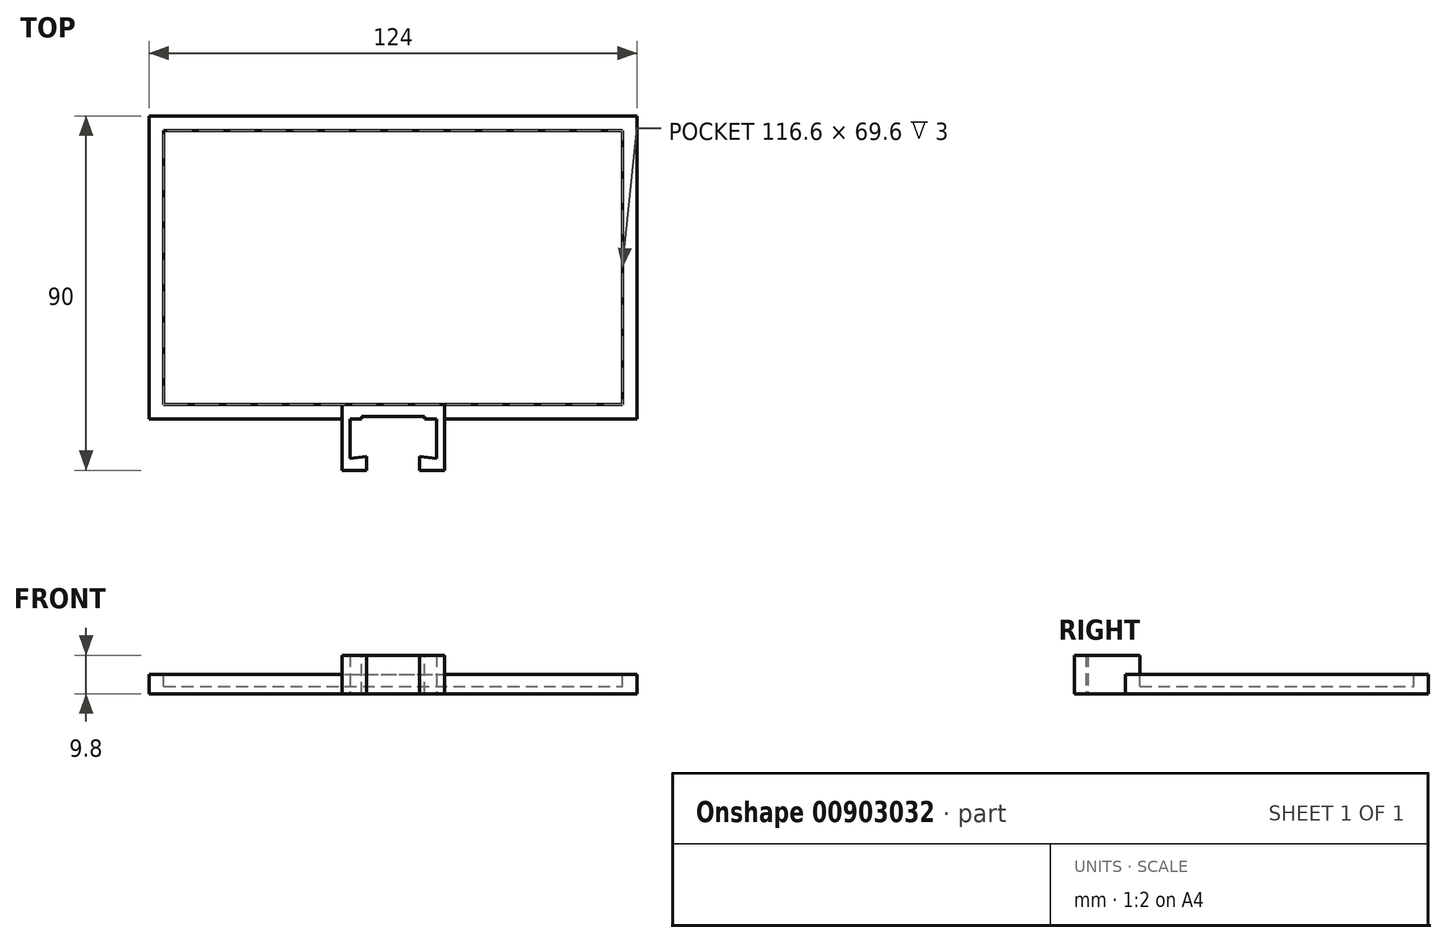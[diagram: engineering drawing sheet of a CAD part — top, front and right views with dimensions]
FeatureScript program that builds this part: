
annotation { "Feature Type Name" : "Feature", "Feature Type Description" : "" }
export const myFeature = defineFeature(function(context is Context, id is Id, definition is map)
    precondition{}
    {
        {
            var Q0;
            Q0=qCreatedBy(makeId("Top.planeOp"),FACE);
            var sketch = newSketch(context, id + "F0", { "sketchPlane" : qUnion([Q0])});
            skLineSegment(sketch, "E0.bottom", {"start": v(0, 0) * mm, "end": v(124, 0) * mm});
            skLineSegment(sketch, "E0.top", {"start": v(0, 77) * mm, "end": v(124, 77) * mm});
            skLineSegment(sketch, "E0.left", {"start": v(0, 0) * mm, "end": v(0, 77) * mm});
            skLineSegment(sketch, "E0.right", {"start": v(124, 0) * mm, "end": v(124, 77) * mm});
            skSolve(sketch);
        }
        {
            var Q0;
            Q0=makeQuery(id+"F0.imprint","IMPRINT",FACE,{"disambiguationData":[TD([[makeQuery(id+"F0.imprint","IMPRINT",EDGE,{"derivedFrom":sQuery(id+"F0.wireOp",EDGE,"E0.bottom")}),1.0]])]});
            extrude(context, id + "F1", {"entities" : qUnion([Q0]), "depth" : 4.9 * mm, "offsetDistance" : 25 * mm});
        }
        {
            var Q0;
            Q0=makeQuery(id+"F1.opExtrude","CAP_FACE",FACE,{"disambiguationData":[OSD([sQuery(id+"F0.wireOp",EDGE,"E0.bottom"),sQuery(id+"F0.wireOp",EDGE,"E0.top"),sQuery(id+"F0.wireOp",EDGE,"E0.left"),sQuery(id+"F0.wireOp",EDGE,"E0.right")])],"isStart":false});
            var sketch = newSketch(context, id + "F2", { "sketchPlane" : qUnion([Q0])});
            skLineSegment(sketch, "E1.0", {"start": v(3.7, 3.7) * mm, "end": v(120.3, 3.7) * mm});
            skLineSegment(sketch, "E1.1", {"start": v(3.7, 3.7) * mm, "end": v(3.7, 73.3) * mm});
            skLineSegment(sketch, "E1.2", {"start": v(3.7, 73.3) * mm, "end": v(120.3, 73.3) * mm});
            skLineSegment(sketch, "E1.3", {"start": v(120.3, 3.7) * mm, "end": v(120.3, 73.3) * mm});
            skSolve(sketch);
        }
        {
            var Q0;
            Q0=makeQuery(id+"F2.imprint","IMPRINT",FACE,{"disambiguationData":[TD([[makeQuery(id+"F2.imprint","IMPRINT",EDGE,{"derivedFrom":sQuery(id+"F2.wireOp",EDGE,"E1.0")}),1.0]])]});
            extrude(context, id + "F3", {"entities" : qUnion([Q0]), "operationType" : NewBodyOperationType.REMOVE, "oppositeDirection" : true, "depth" : 3 * mm, "offsetDistance" : 25 * mm});
        }
        {
            var Q0;
            Q0=qCreatedBy(makeId("Top.planeOp"),FACE);
            var sketch = newSketch(context, id + "F4", { "sketchPlane" : qUnion([Q0])});
            skLineSegment(sketch, "E2.0", {"start": v(0, 0) * mm, "end": v(124, 0) * mm, "construction": true});
            skPoint(sketch, "E3", {"position": v(62, 0) * mm});
            skLineSegment(sketch, "E4", {"start": v(51, 0) * mm, "end": v(51, -10) * mm});
            skLineSegment(sketch, "E5", {"start": v(51, -10) * mm, "end": v(55.25, -9.5) * mm});
            skLineSegment(sketch, "E6", {"start": v(55.25, -9.5) * mm, "end": v(55.25, -13) * mm});
            skLineSegment(sketch, "E7", {"start": v(55.25, -13) * mm, "end": v(49, -13) * mm});
            skLineSegment(sketch, "E8", {"start": v(49, -13) * mm, "end": v(49, -13) * mm});
            skLineSegment(sketch, "E9", {"start": v(49, -13) * mm, "end": v(49, 0) * mm});
            skLineSegment(sketch, "E10", {"start": v(49, 0) * mm, "end": v(49, 0) * mm});
            skLineSegment(sketch, "E11", {"start": v(51, 0) * mm, "end": v(49, 0) * mm});
            skLineSegment(sketch, "E12", {"start": v(62, 0) * mm, "end": v(62, -37.08) * mm, "construction": true});
            skLineSegment(sketch, "E13.MirrorCS", {"start": v(68.75, -13) * mm, "end": v(75, -13) * mm});
            skLineSegment(sketch, "E14.MirrorCS", {"start": v(68.75, -9.5) * mm, "end": v(68.75, -13) * mm});
            skLineSegment(sketch, "E15.MirrorCS", {"start": v(73, -10) * mm, "end": v(68.75, -9.5) * mm});
            skLineSegment(sketch, "E16.MirrorCS", {"start": v(73, 0) * mm, "end": v(73, -10) * mm});
            skLineSegment(sketch, "E17.MirrorCS", {"start": v(75, -13) * mm, "end": v(75, 0) * mm});
            skLineSegment(sketch, "E18.MirrorCS", {"start": v(73, 0) * mm, "end": v(75, 0) * mm});
            skSolve(sketch);
        }
        {
            var Q0;
            Q0=makeQuery(id+"F4.imprint","IMPRINT",FACE,{"disambiguationData":[TD([[makeQuery(id+"F4.imprint","IMPRINT",EDGE,{"derivedFrom":sQuery(id+"F4.wireOp",EDGE,"E4")}),-1.0]])]});
            var Q1;
            Q1=makeQuery(id+"F4.imprint","IMPRINT",FACE,{"disambiguationData":[TD([[makeQuery(id+"F4.imprint","IMPRINT",EDGE,{"derivedFrom":sQuery(id+"F4.wireOp",EDGE,"E13.MirrorCS")}),1.0]])]});
            extrude(context, id + "F5", {"entities" : qUnion([Q0, Q1]), "operationType" : NewBodyOperationType.ADD, "depth" : 9.8 * mm, "offsetDistance" : 25 * mm});
        }
        {
            var Q0;
            Q0=makeQuery(id+"F1.opExtrude","CAP_FACE",FACE,{"disambiguationData":[OSD([sQuery(id+"F0.wireOp",EDGE,"E0.bottom"),sQuery(id+"F0.wireOp",EDGE,"E0.top"),sQuery(id+"F0.wireOp",EDGE,"E0.left"),sQuery(id+"F0.wireOp",EDGE,"E0.right")])],"isStart":false});
            var sketch = newSketch(context, id + "F6", { "sketchPlane" : qUnion([Q0])});
            skLineSegment(sketch, "E19", {"start": v(49, 0) * mm, "end": v(49, 3.7) * mm});
            skLineSegment(sketch, "E20", {"start": v(49, 3.7) * mm, "end": v(75, 3.7) * mm});
            skLineSegment(sketch, "E21", {"start": v(75, 3.7) * mm, "end": v(75, 0) * mm});
            skLineSegment(sketch, "E22", {"start": v(75, 0) * mm, "end": v(49, 0) * mm});
            skSolve(sketch);
        }
        {
            var Q0;
            {var subQ2=sQuery(id+"F6.wireOp",EDGE,"E19");Q0=makeQuery(id+"F6.imprint","IMPRINT",FACE,{"disambiguationData":[TD([[makeQuery(id+"F6.imprint","IMPRINT",EDGE,{"derivedFrom":subQ2}),-1.0]])]});}
            var Q1;
            Q1=makeQuery(id+"F5.opExtrude","CAP_FACE",FACE,{"disambiguationData":[OSD([sQuery(id+"F4.wireOp",EDGE,"E4"),sQuery(id+"F4.wireOp",EDGE,"E5"),sQuery(id+"F4.wireOp",EDGE,"E6"),sQuery(id+"F4.wireOp",EDGE,"E7"),sQuery(id+"F4.wireOp",EDGE,"E9"),sQuery(id+"F4.wireOp",EDGE,"E11")])],"isStart":false});
            extrude(context, id + "F7", {"entities" : qUnion([Q0]), "operationType" : NewBodyOperationType.ADD, "endBound" : BoundingType.UP_TO_SURFACE, "depth" : 25 * mm, "endBoundEntityFace" : qUnion([Q1]), "offsetDistance" : 25 * mm});
        }
        {
            var Q0;
            Q0=makeQuery(id+"F7.boolean.opBoolean","MERGE",FACE,{"derivedFrom":[makeQuery(id+"F5.opExtrude","CAP_FACE",FACE,{"disambiguationData":[OSD([sQuery(id+"F4.wireOp",EDGE,"E4"),sQuery(id+"F4.wireOp",EDGE,"E5"),sQuery(id+"F4.wireOp",EDGE,"E6"),sQuery(id+"F4.wireOp",EDGE,"E7"),sQuery(id+"F4.wireOp",EDGE,"E9"),sQuery(id+"F4.wireOp",EDGE,"E11")])],"isStart":false}),makeQuery(id+"F5.opExtrude","CAP_FACE",FACE,{"disambiguationData":[OSD([sQuery(id+"F4.wireOp",EDGE,"E13.MirrorCS"),sQuery(id+"F4.wireOp",EDGE,"E14.MirrorCS"),sQuery(id+"F4.wireOp",EDGE,"E15.MirrorCS"),sQuery(id+"F4.wireOp",EDGE,"E16.MirrorCS"),sQuery(id+"F4.wireOp",EDGE,"E17.MirrorCS"),sQuery(id+"F4.wireOp",EDGE,"E18.MirrorCS")])],"isStart":false}),makeQuery(id+"F7.opExtrude","CAP_FACE",FACE,{"disambiguationData":[OSD([sQuery(id+"F6.wireOp",EDGE,"E19"),sQuery(id+"F6.wireOp",EDGE,"E20"),sQuery(id+"F6.wireOp",EDGE,"E21"),sQuery(id+"F6.wireOp",EDGE,"E22")])],"isStart":false})]});
            var sketch = newSketch(context, id + "F8", { "sketchPlane" : qUnion([Q0])});
            skLineSegment(sketch, "E23.bottom", {"start": v(54, 0) * mm, "end": v(70, 0) * mm});
            skLineSegment(sketch, "E23.top", {"start": v(54, 0.7) * mm, "end": v(70, 0.7) * mm});
            skLineSegment(sketch, "E23.left", {"start": v(54, 0) * mm, "end": v(54, 0.7) * mm});
            skLineSegment(sketch, "E23.right", {"start": v(70, 0) * mm, "end": v(70, 0.7) * mm});
            skPoint(sketch, "E24", {"position": v(62, 0) * mm});
            skSolve(sketch);
        }
        {
            var Q0;
            Q0=makeQuery(id+"F8.imprint","IMPRINT",FACE,{"disambiguationData":[TD([[makeQuery(id+"F8.imprint","IMPRINT",EDGE,{"derivedFrom":sQuery(id+"F8.wireOp",EDGE,"E23.bottom")}),1.0]])]});
            extrude(context, id + "F9", {"entities" : qUnion([Q0]), "operationType" : NewBodyOperationType.REMOVE, "oppositeDirection" : true, "depth" : 25 * mm, "offsetDistance" : 25 * mm});
        }
    });
